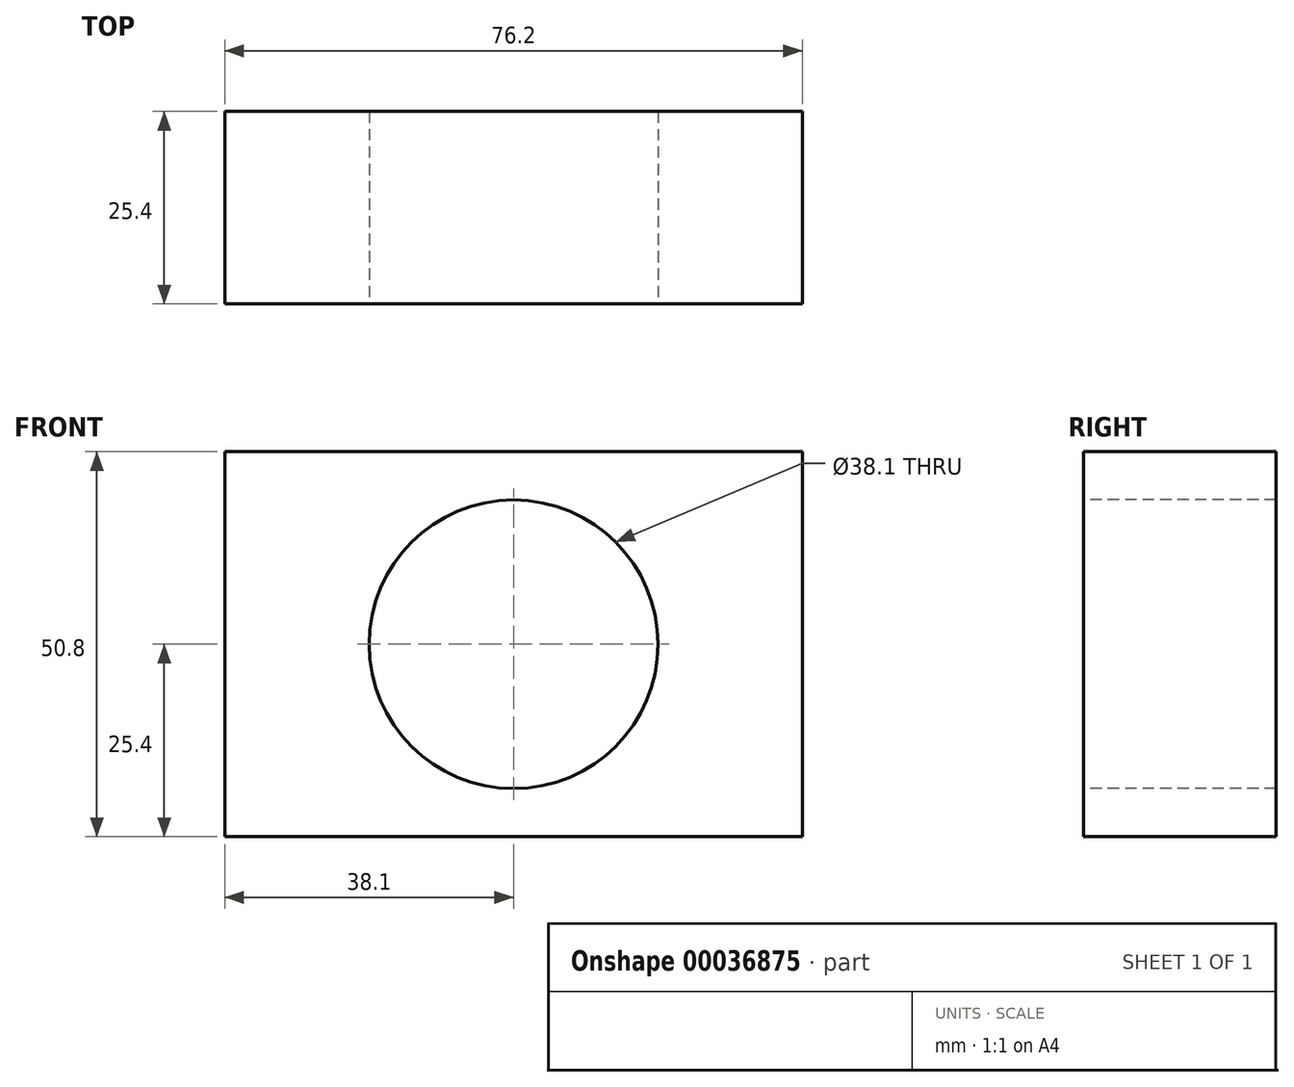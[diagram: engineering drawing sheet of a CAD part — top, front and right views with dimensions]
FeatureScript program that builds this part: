
annotation { "Feature Type Name" : "Feature", "Feature Type Description" : "" }
export const myFeature = defineFeature(function(context is Context, id is Id, definition is map)
    precondition{}
    {
        {
            var Q0;
            Q0=qCreatedBy(makeId("Front.planeOp"),FACE);
            var sketch = newSketch(context, id + "F0", { "sketchPlane" : qUnion([Q0])});
            skLineSegment(sketch, "E0.bottom", {"start": v(0, 50.8) * mm, "end": v(76.2, 50.8) * mm});
            skLineSegment(sketch, "E0.top", {"start": v(0, 0) * mm, "end": v(76.2, 0) * mm});
            skLineSegment(sketch, "E0.left", {"start": v(0, 50.8) * mm, "end": v(0, 0) * mm});
            skLineSegment(sketch, "E0.right", {"start": v(76.2, 50.8) * mm, "end": v(76.2, 0) * mm});
            skSolve(sketch);
        }
        {
            var Q0;
            Q0 = qSketchRegion(id + "F0", true);
            extrude(context, id + "F1", {"entities" : qUnion([Q0]), "endBound" : BoundingType.SYMMETRIC, "depth" : 25.4 * mm});
        }
        {
            var Q0;
            Q0=makeQuery(id+"F1.opExtrude","CAP_FACE",FACE,{"disambiguationData":[OSD([sQuery(id+"F0.wireOp",EDGE,"E0.bottom"),sQuery(id+"F0.wireOp",EDGE,"E0.top"),sQuery(id+"F0.wireOp",EDGE,"E0.left"),sQuery(id+"F0.wireOp",EDGE,"E0.right")])],"isStart":false});
            var sketch = newSketch(context, id + "F2", { "sketchPlane" : qUnion([Q0])});
            skPoint(sketch, "E1", {"position": v(38.1, 25.4) * mm});
            skLineSegment(sketch, "E2", {"start": v(38.1, 50.8) * mm, "end": v(38.1, 0) * mm, "construction": true});
            skSolve(sketch);
        }
        {
            var Q0;
            Q0=sQuery(id+"F2.wireOp",VERTEX,"E1");
            var Q1;
            Q1=makeQuery(id+"F1.opExtrude","SWEPT_BODY",BODY,{"disambiguationData":[OSD([sQuery(id+"F0.wireOp",EDGE,"E0.bottom"),sQuery(id+"F0.wireOp",EDGE,"E0.top"),sQuery(id+"F0.wireOp",EDGE,"E0.left"),sQuery(id+"F0.wireOp",EDGE,"E0.right")])]});
            hole(context, id + "F3", {"style" : HoleStyle.SIMPLE, "holeDiameter" : 38.1 * mm, "endStyle" : HoleEndStyle.THROUGH, "locations" : qUnion([Q0]), "scope" : qUnion([Q1])});
        }
    });
